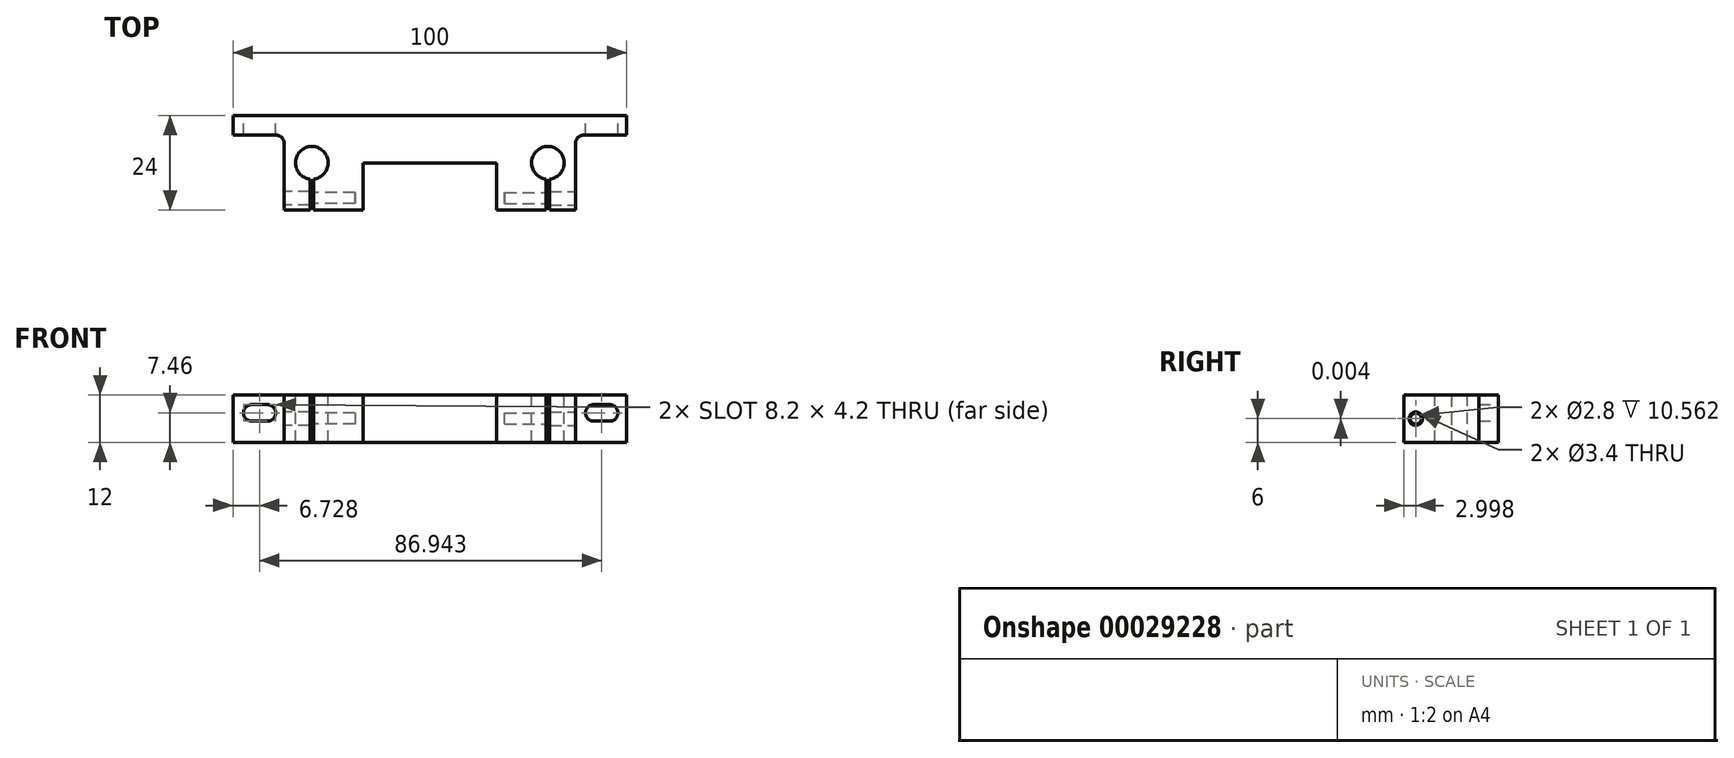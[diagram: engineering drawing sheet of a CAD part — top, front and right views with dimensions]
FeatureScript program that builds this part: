
annotation { "Feature Type Name" : "Feature", "Feature Type Description" : "" }
export const myFeature = defineFeature(function(context is Context, id is Id, definition is map)
    precondition{}
    {
        {
            var Q0;
            Q0=qCreatedBy(makeId("Top.planeOp"),FACE);
            var sketch = newSketch(context, id + "F0", { "sketchPlane" : qUnion([Q0])});
            skLineSegment(sketch, "E0", {"start": v(-46.35, 12.3) * mm, "end": v(53.65, 12.3) * mm});
            skLineSegment(sketch, "E1", {"start": v(53.65, 12.3) * mm, "end": v(53.65, 7.3) * mm});
            skLineSegment(sketch, "E2", {"start": v(53.65, 7.3) * mm, "end": v(40.65, 7.3) * mm});
            skLineSegment(sketch, "E3", {"start": v(40.65, 7.3) * mm, "end": v(40.65, -11.7) * mm});
            skLineSegment(sketch, "E4", {"start": v(-33.35, -11.7) * mm, "end": v(-33.35, 7.3) * mm});
            skLineSegment(sketch, "E5", {"start": v(-33.35, 7.3) * mm, "end": v(-46.35, 7.3) * mm});
            skLineSegment(sketch, "E6", {"start": v(-46.35, 7.3) * mm, "end": v(-46.35, 12.3) * mm});
            skLineSegment(sketch, "E7.top", {"start": v(-13.35, 0.3) * mm, "end": v(20.65, 0.3) * mm});
            skLineSegment(sketch, "E7.left", {"start": v(-13.35, -11.7) * mm, "end": v(-13.35, 0.3) * mm});
            skLineSegment(sketch, "E7.right", {"start": v(20.65, -11.7) * mm, "end": v(20.65, 0.3) * mm});
            skLineSegment(sketch, "E8", {"start": v(-33.35, -11.7) * mm, "end": v(-13.35, -11.7) * mm});
            skLineSegment(sketch, "E9", {"start": v(20.65, -11.7) * mm, "end": v(40.65, -11.7) * mm});
            skSolve(sketch);
        }
        {
            var Q0;
            Q0=qSketchRegion(id+"F0",true);
            extrude(context, id + "F1", {"entities" : qUnion([Q0]), "depth" : 12 * mm});
        }
        {
            var Q0;
            Q0=makeQuery(id+"F1.opExtrude","CAP_FACE",FACE,{"disambiguationData":[OSD([sQuery(id+"F0.wireOp",EDGE,"E0"),sQuery(id+"F0.wireOp",EDGE,"E1"),sQuery(id+"F0.wireOp",EDGE,"E2"),sQuery(id+"F0.wireOp",EDGE,"E3"),sQuery(id+"F0.wireOp",EDGE,"a543b13f-e40b-4fbf-b45e-1d40242ad481"),sQuery(id+"F0.wireOp",EDGE,"E4"),sQuery(id+"F0.wireOp",EDGE,"E5"),sQuery(id+"F0.wireOp",EDGE,"E6")])],"isStart":false});
            var sketch = newSketch(context, id + "F2", { "sketchPlane" : qUnion([Q0])});
            skCircle(sketch, "E10", {"center": v(-26.35, 0.3) * mm, "radius": 4.15 * mm});
            skCircle(sketch, "E11", {"center": v(33.65, 0.3) * mm, "radius": 4.15 * mm});
            skPoint(sketch, "E12", {"position": v(3.65, 12.3) * mm});
            skLineSegment(sketch, "E13.bottom", {"start": v(33.21, -3.01) * mm, "end": v(34.09, -3.01) * mm});
            skLineSegment(sketch, "E13.top", {"start": v(33.21, -12.27) * mm, "end": v(34.09, -12.27) * mm});
            skLineSegment(sketch, "E13.left", {"start": v(33.21, -3.01) * mm, "end": v(33.21, -12.27) * mm});
            skLineSegment(sketch, "E13.right", {"start": v(34.09, -3.01) * mm, "end": v(34.09, -12.27) * mm});
            skPoint(sketch, "E14", {"position": v(33.65, -3.01) * mm});
            skLineSegment(sketch, "E15", {"start": v(3.65, 12.3) * mm, "end": v(3.65, -11.7) * mm, "construction": true});
            skLineSegment(sketch, "E16.MirrorCS", {"start": v(-25.91, -12.27) * mm, "end": v(-26.79, -12.27) * mm});
            skLineSegment(sketch, "E17.MirrorCS", {"start": v(-26.79, -3.01) * mm, "end": v(-26.79, -12.27) * mm});
            skLineSegment(sketch, "E18.MirrorCS", {"start": v(-25.91, -3.01) * mm, "end": v(-26.79, -3.01) * mm});
            skLineSegment(sketch, "E19.MirrorCS", {"start": v(-25.91, -3.01) * mm, "end": v(-25.91, -12.27) * mm});
            skSolve(sketch);
        }
        {
            var Q0;
            Q0=qSketchRegion(id+"F2",true);
            var Q1;
            {var subQ3=sQuery(id+"F2.wireOp",EDGE,"E13.bottom");Q1=makeQuery(id+"F2.imprint","IMPRINT",FACE,{"disambiguationData":[TD([[makeQuery(id+"F2.imprint","IMPRINT",EDGE,{"derivedFrom":subQ3}),-1.0]])]});}
            var Q2;
            {var subQ3=sQuery(id+"F2.wireOp",EDGE,"E18.MirrorCS");Q2=makeQuery(id+"F2.imprint","IMPRINT",FACE,{"disambiguationData":[TD([[makeQuery(id+"F2.imprint","IMPRINT",EDGE,{"derivedFrom":subQ3}),1.0]])]});}
            extrude(context, id + "F3", {"entities" : qUnion([Q0, Q1, Q2]), "operationType" : NewBodyOperationType.REMOVE, "endBound" : BoundingType.THROUGH_ALL, "oppositeDirection" : true, "depth" : 25 * mm});
        }
        {
            var Q0;
            Q0=makeQuery(id+"F1.opExtrude","SWEPT_FACE",FACE,{"disambiguationData":[OSD([sQuery(id+"F0.wireOp",EDGE,"E0")])]});
            var sketch = newSketch(context, id + "F4", { "sketchPlane" : qUnion([Q0])});
            skLineSegment(sketch, "E20", {"start": v(-53.65, 7.46) * mm, "end": v(46.35, 7.46) * mm, "construction": true});
            skLineSegment(sketch, "E21.bottom", {"start": v(-49.32, 9.56) * mm, "end": v(-45.32, 9.56) * mm});
            skLineSegment(sketch, "E21.top", {"start": v(-49.32, 5.36) * mm, "end": v(-45.32, 5.36) * mm});
            skArc(sketch, "E22", {"start": v(-45.32, 5.36) * mm, "mid": v(-43.22, 7.46) * mm, "end": v(-45.32, 9.56) * mm});
            skArc(sketch, "E23", {"start": v(-49.32, 9.56) * mm, "mid": v(-51.42, 7.46) * mm, "end": v(-49.32, 5.36) * mm});
            skLineSegment(sketch, "E24.top", {"start": v(37.62, 5.36) * mm, "end": v(41.62, 5.36) * mm});
            skLineSegment(sketch, "E24.bottom", {"start": v(37.62, 9.56) * mm, "end": v(41.62, 9.56) * mm});
            skArc(sketch, "E25", {"start": v(37.62, 9.56) * mm, "mid": v(35.52, 7.46) * mm, "end": v(37.62, 5.36) * mm});
            skArc(sketch, "E26", {"start": v(41.62, 5.36) * mm, "mid": v(43.72, 7.46) * mm, "end": v(41.62, 9.56) * mm});
            skSolve(sketch);
        }
        {
            var Q0;
            Q0=qSketchRegion(id+"F4",true);
            extrude(context, id + "F5", {"entities" : qUnion([Q0]), "operationType" : NewBodyOperationType.REMOVE, "endBound" : BoundingType.THROUGH_ALL, "oppositeDirection" : true, "depth" : 25 * mm});
        }
        {
            var Q0;
            Q0=makeQuery(id+"F1.opExtrude","SWEPT_FACE",FACE,{"disambiguationData":[OSD([sQuery(id+"F0.wireOp",EDGE,"a543b13f-e40b-4fbf-b45e-1d40242ad481")])]});
            var sketch = newSketch(context, id + "F6", { "sketchPlane" : qUnion([Q0])});
            skLineSegment(sketch, "E27", {"start": v(-33.35, 6) * mm, "end": v(40.65, 6) * mm, "construction": true});
            skCircle(sketch, "E28", {"center": v(6.65, 6) * mm, "radius": 4.1 * mm});
            skSolve(sketch);
        }
        {
            var Q0;
            Q0=makeQuery(id+"F1.opExtrude","CAP_FACE",FACE,{"disambiguationData":[OSD([sQuery(id+"F0.wireOp",EDGE,"E0"),sQuery(id+"F0.wireOp",EDGE,"E1"),sQuery(id+"F0.wireOp",EDGE,"E2"),sQuery(id+"F0.wireOp",EDGE,"E3"),sQuery(id+"F0.wireOp",EDGE,"a543b13f-e40b-4fbf-b45e-1d40242ad481"),sQuery(id+"F0.wireOp",EDGE,"E4"),sQuery(id+"F0.wireOp",EDGE,"E5"),sQuery(id+"F0.wireOp",EDGE,"E6")])],"isStart":false});
            var sketch = newSketch(context, id + "F7", { "sketchPlane" : qUnion([Q0])});
            skLineSegment(sketch, "E29.bottom", {"start": v(-7.35, 0.3) * mm, "end": v(20.65, 0.3) * mm});
            skLineSegment(sketch, "E29.top", {"start": v(-7.35, -7.7) * mm, "end": v(20.65, -7.7) * mm});
            skLineSegment(sketch, "E29.left", {"start": v(-7.35, 0.3) * mm, "end": v(-7.35, -7.7) * mm});
            skLineSegment(sketch, "E29.right", {"start": v(20.65, 0.3) * mm, "end": v(20.65, -7.7) * mm});
            skLineSegment(sketch, "E30", {"start": v(6.65, 12.3) * mm, "end": v(6.65, -11.7) * mm, "construction": true});
            skLineSegment(sketch, "E31", {"start": v(6.65, 0.3) * mm, "end": v(6.65, -7.7) * mm});
            skSolve(sketch);
        }
        {
            var Q0;
            Q0=makeQuery(id+"FkOM364ZJOPxlfX_1.boolean.opBoolean","COPY",FACE,{"derivedFrom":makeQuery(id+"FkOM364ZJOPxlfX_1.opExtrude","SWEPT_FACE",FACE,{"disambiguationData":[OSD([sQuery(id+"F7.wireOp",EDGE,"E29.bottom")])]})});
            var sketch = newSketch(context, id + "F8", { "sketchPlane" : qUnion([Q0])});
            skCircle(sketch, "E32", {"center": v(-3.35, 6) * mm, "radius": 5.2 * mm});
            skSolve(sketch);
        }
        {
            var Q0;
            Q0=makeQuery(id+"FkOM364ZJOPxlfX_1.boolean.opBoolean","COPY",FACE,{"derivedFrom":makeQuery(id+"FkOM364ZJOPxlfX_1.opExtrude","SWEPT_FACE",FACE,{"disambiguationData":[OSD([sQuery(id+"F7.wireOp",EDGE,"E29.top")])]})});
            var sketch = newSketch(context, id + "F9", { "sketchPlane" : qUnion([Q0])});
            skCircle(sketch, "E33", {"center": v(3.35, 6) * mm, "radius": 5.25 * mm});
            skSolve(sketch);
        }
        {
            var Q0;
            Q0=makeQuery(id+"F1.opExtrude","CAP_FACE",FACE,{"disambiguationData":[OSD([sQuery(id+"F0.wireOp",EDGE,"E0"),sQuery(id+"F0.wireOp",EDGE,"E1"),sQuery(id+"F0.wireOp",EDGE,"E2"),sQuery(id+"F0.wireOp",EDGE,"E3"),sQuery(id+"F0.wireOp",EDGE,"a543b13f-e40b-4fbf-b45e-1d40242ad481"),sQuery(id+"F0.wireOp",EDGE,"E4"),sQuery(id+"F0.wireOp",EDGE,"E5"),sQuery(id+"F0.wireOp",EDGE,"E6")])],"isStart":false});
            var sketch = newSketch(context, id + "F10", { "sketchPlane" : qUnion([Q0])});
            skText(sketch, "E34", { "text": "T", "fontName": "OpenSans-Regular.ttf"});
            const initialGuessF10  = {"E34": [-0.02337, -0.0117, 1, 0, 0.024]};
            skSetInitialGuess(sketch, initialGuessF10);
            skSolve(sketch);
        }
        {
            var Q0;
            Q0=makeQuery(id+"F1.opExtrude","SWEPT_FACE",FACE,{"disambiguationData":[OSD([sQuery(id+"F0.wireOp",EDGE,"E3")])]});
            var sketch = newSketch(context, id + "F11", { "sketchPlane" : qUnion([Q0])});
            skCircle(sketch, "E35", {"center": v(-8.7, 6) * mm, "radius": 1.7 * mm});
            skCircle(sketch, "E36", {"center": v(-8.7, 6) * mm, "radius": 1.4 * mm});
            skLineSegment(sketch, "E37", {"start": v(7.3, 6) * mm, "end": v(15.16, 6) * mm, "construction": true});
            skSolve(sketch);
        }
        {
            var Q0;
            Q0=makeQuery(id+"F11.imprint","IMPRINT",FACE,{"disambiguationData":[TD([[makeQuery(id+"F11.imprint","IMPRINT",EDGE,{"derivedFrom":sQuery(id+"F11.wireOp",EDGE,"E36")}),1.0]])]});
            extrude(context, id + "F12", {"entities" : qUnion([Q0]), "operationType" : NewBodyOperationType.REMOVE, "oppositeDirection" : true, "depth" : 18 * mm});
        }
        {
            var Q0;
            Q0=makeQuery(id+"F11.imprint","IMPRINT",FACE,{"disambiguationData":[TD([[makeQuery(id+"F11.imprint","IMPRINT",EDGE,{"derivedFrom":sQuery(id+"F11.wireOp",EDGE,"E36")}),1.0]])]});
            var Q1;
            Q1=makeQuery(id+"F11.imprint","IMPRINT",FACE,{"disambiguationData":[TD([[makeQuery(id+"F11.imprint","IMPRINT",EDGE,{"derivedFrom":sQuery(id+"F11.wireOp",EDGE,"E35")}),1.0]])]});
            extrude(context, id + "F13", {"entities" : qUnion([Q0, Q1]), "operationType" : NewBodyOperationType.REMOVE, "endBound" : BoundingType.UP_TO_NEXT, "oppositeDirection" : true, "depth" : 7 * mm});
        }
        {
            var Q0;
            Q0=makeQuery(id+"F1.opExtrude","SWEPT_EDGE",EDGE,{"disambiguationData":[OSD([sQuery(id+"F0.wireOp",EDGE,"E2"),sQuery(id+"F0.wireOp",EDGE,"E3")])]});
            fillet(context, id + "F14", {"entities" : qUnion([Q0]), "radius" : 2 * mm, "tangentPropagation" : true, "allowEdgeOverflow" : false});
        }
        {
            var Q0;
            Q0=makeQuery(id+"F1.opExtrude","SWEPT_FACE",FACE,{"disambiguationData":[OSD([sQuery(id+"F0.wireOp",EDGE,"E4")])]});
            var sketch = newSketch(context, id + "F15", { "sketchPlane" : qUnion([Q0])});
            skCircle(sketch, "E38", {"center": v(8.7, 6) * mm, "radius": 1.7 * mm});
            skCircle(sketch, "E39", {"center": v(8.7, 6) * mm, "radius": 1.4 * mm});
            skLineSegment(sketch, "E40", {"start": v(8.7, 0) * mm, "end": v(8.7, 12) * mm, "construction": true});
            skSolve(sketch);
        }
        {
            var Q0;
            Q0=makeQuery(id+"F15.imprint","IMPRINT",FACE,{"disambiguationData":[TD([[makeQuery(id+"F15.imprint","IMPRINT",EDGE,{"derivedFrom":sQuery(id+"F15.wireOp",EDGE,"E39")}),1.0]])]});
            extrude(context, id + "F16", {"entities" : qUnion([Q0]), "operationType" : NewBodyOperationType.REMOVE, "oppositeDirection" : true, "depth" : 18 * mm});
        }
        {
            var Q0;
            Q0=makeQuery(id+"F15.imprint","IMPRINT",FACE,{"disambiguationData":[TD([[makeQuery(id+"F15.imprint","IMPRINT",EDGE,{"derivedFrom":sQuery(id+"F15.wireOp",EDGE,"E39")}),1.0]])]});
            var Q1;
            Q1=makeQuery(id+"F15.imprint","IMPRINT",FACE,{"disambiguationData":[TD([[makeQuery(id+"F15.imprint","IMPRINT",EDGE,{"derivedFrom":sQuery(id+"F15.wireOp",EDGE,"E38")}),1.0]])]});
            extrude(context, id + "F17", {"entities" : qUnion([Q0, Q1]), "operationType" : NewBodyOperationType.REMOVE, "endBound" : BoundingType.UP_TO_NEXT, "oppositeDirection" : true, "depth" : 25 * mm});
        }
        {
            var Q0;
            Q0=makeQuery(id+"F1.opExtrude","SWEPT_EDGE",EDGE,{"disambiguationData":[OSD([sQuery(id+"F0.wireOp",EDGE,"E4"),sQuery(id+"F0.wireOp",EDGE,"E5")])]});
            fillet(context, id + "F18", {"entities" : qUnion([Q0]), "radius" : 2 * mm, "tangentPropagation" : true, "allowEdgeOverflow" : false});
        }
    });
